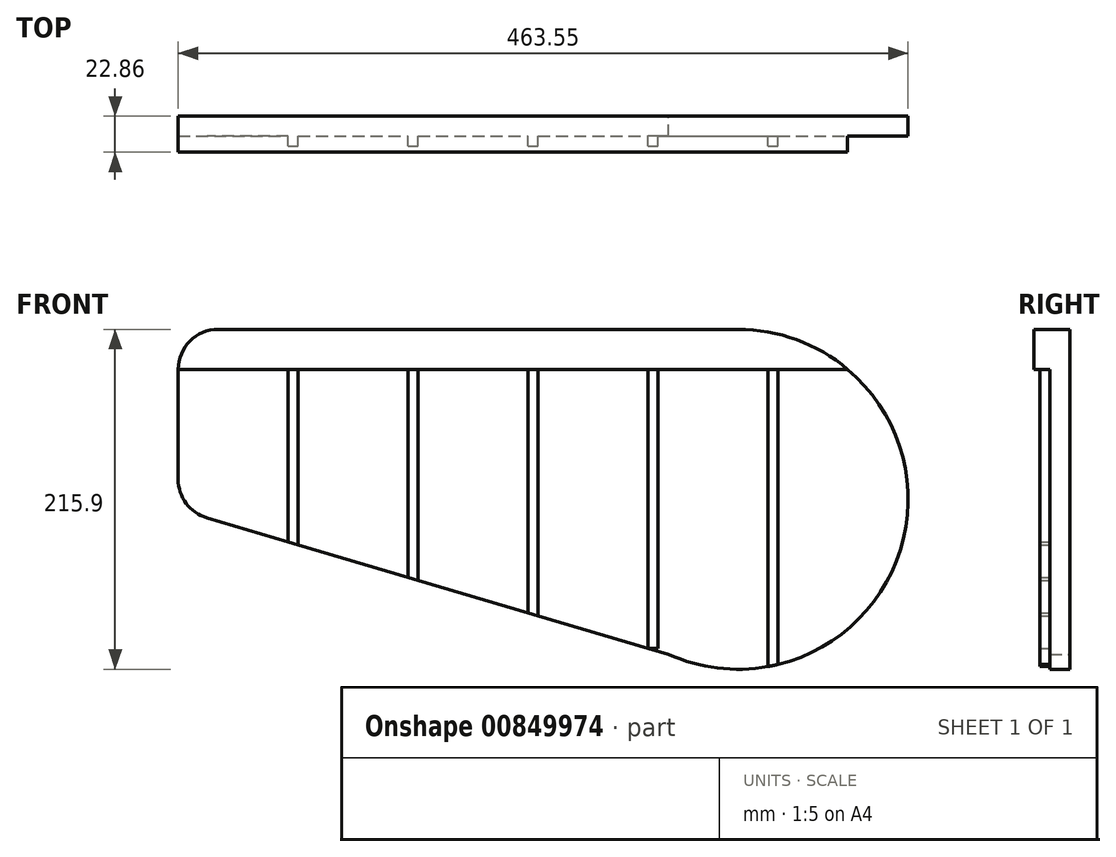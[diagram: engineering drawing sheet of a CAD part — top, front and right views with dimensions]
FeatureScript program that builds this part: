
annotation { "Feature Type Name" : "Feature", "Feature Type Description" : "" }
export const myFeature = defineFeature(function(context is Context, id is Id, definition is map)
    precondition{}
    {
        {
            var Q0;
            Q0=qCreatedBy(makeId("Front.planeOp"),FACE);
            var sketch = newSketch(context, id + "F0", { "sketchPlane" : qUnion([Q0])});
            skLineSegment(sketch, "E0", {"start": v(0, 18.97) * mm, "end": v(0, 88.9) * mm});
            skLineSegment(sketch, "E1", {"start": v(25.4, 114.3) * mm, "end": v(355.6, 114.3) * mm});
            skLineSegment(sketch, "E2", {"start": v(311.37, -92.12) * mm, "end": v(18.2, -5.38) * mm});
            skArc(sketch, "E3", {"start": v(311.37, -92.12) * mm, "mid": v(461.15, -16.27) * mm, "end": v(355.6, 114.3) * mm});
            skPoint(sketch, "E4.visualSharp", {"position": v(0, 114.3) * mm});
            skArc(sketch, "E4.filletArc", {"start": v(25.4, 114.3) * mm, "mid": v(7.44, 106.86) * mm, "end": v(0, 88.9) * mm});
            skPoint(sketch, "E5.visualSharp", {"position": v(0, 0) * mm});
            skArc(sketch, "E5.filletArc", {"start": v(0, 18.97) * mm, "mid": v(5.05, 3.77) * mm, "end": v(18.2, -5.38) * mm});
            skSolve(sketch);
        }
        {
            var Q0;
            Q0=makeQuery(id+"F0.imprint","IMPRINT",FACE,{"disambiguationData":[TD([[makeQuery(id+"F0.imprint","IMPRINT",EDGE,{"derivedFrom":sQuery(id+"F0.wireOp",EDGE,"E0")}),-1.0]])]});
            extrude(context, id + "F1", {"entities" : qUnion([Q0]), "depth" : 12.7 * mm, "offsetDistance" : 25.4 * mm});
        }
        {
            var Q0;
            Q0=makeQuery(id+"F1.opExtrude","CAP_FACE",FACE,{"disambiguationData":[OSD([sQuery(id+"F0.wireOp",EDGE,"E0"),sQuery(id+"F0.wireOp",EDGE,"E1"),sQuery(id+"F0.wireOp",EDGE,"E2"),sQuery(id+"F0.wireOp",EDGE,"E3"),sQuery(id+"F0.wireOp",EDGE,"E4.filletArc"),sQuery(id+"F0.wireOp",EDGE,"E5.filletArc")])],"isStart":false});
            var sketch = newSketch(context, id + "F2", { "sketchPlane" : qUnion([Q0])});
            skLineSegment(sketch, "E6", {"start": v(0, 88.9) * mm, "end": v(425.16, 88.9) * mm});
            skSolve(sketch);
        }
        {
            var Q0;
            {var subQ0=sQuery(id+"F2.wireOp",EDGE,"E6");Q0=makeQuery(id+"F2.imprint","IMPRINT",FACE,{"disambiguationData":[TD([[makeQuery(id+"F2.imprint","IMPRINT",EDGE,{"derivedFrom":subQ0}),1.0]])]});}
            extrude(context, id + "F3", {"entities" : qUnion([Q0]), "operationType" : NewBodyOperationType.ADD, "depth" : 10.16 * mm, "offsetDistance" : 25.4 * mm});
        }
        {
            var Q0;
            Q0=makeQuery(id+"F1.opExtrude","CAP_FACE",FACE,{"disambiguationData":[OSD([sQuery(id+"F0.wireOp",EDGE,"E0"),sQuery(id+"F0.wireOp",EDGE,"E1"),sQuery(id+"F0.wireOp",EDGE,"E2"),sQuery(id+"F0.wireOp",EDGE,"E3"),sQuery(id+"F0.wireOp",EDGE,"E4.filletArc"),sQuery(id+"F0.wireOp",EDGE,"E5.filletArc")])],"isStart":false});
            var sketch = newSketch(context, id + "F4", { "sketchPlane" : qUnion([Q0])});
            skPoint(sketch, "E7", {"position": v(0, 88.9) * mm});
            skPoint(sketch, "E8", {"position": v(69.85, 88.9) * mm});
            skPoint(sketch, "E9", {"position": v(76.2, 88.9) * mm});
            skPoint(sketch, "E10", {"position": v(146.05, 88.9) * mm});
            skPoint(sketch, "E11", {"position": v(152.4, 88.9) * mm});
            skPoint(sketch, "E12", {"position": v(222.25, 88.9) * mm});
            skPoint(sketch, "E13", {"position": v(228.6, 88.9) * mm});
            skPoint(sketch, "E14", {"position": v(298.45, 88.9) * mm});
            skPoint(sketch, "E15", {"position": v(304.8, 88.9) * mm});
            skPoint(sketch, "E16", {"position": v(374.65, 88.9) * mm});
            skPoint(sketch, "E17", {"position": v(381, 88.9) * mm});
            skLineSegment(sketch, "E18", {"start": v(69.85, 88.9) * mm, "end": v(76.2, 88.9) * mm});
            skLineSegment(sketch, "E19", {"start": v(69.85, 88.9) * mm, "end": v(69.85, -20.67) * mm});
            skLineSegment(sketch, "E20", {"start": v(76.2, 88.9) * mm, "end": v(76.2, -22.54) * mm});
            skLineSegment(sketch, "E21", {"start": v(69.85, -20.67) * mm, "end": v(76.2, -22.54) * mm});
            skLineSegment(sketch, "E22", {"start": v(146.05, 88.9) * mm, "end": v(146.05, -43.21) * mm});
            skLineSegment(sketch, "E23", {"start": v(152.4, 88.9) * mm, "end": v(152.4, -45.09) * mm});
            skLineSegment(sketch, "E24", {"start": v(152.4, -45.09) * mm, "end": v(146.05, -43.21) * mm});
            skLineSegment(sketch, "E25", {"start": v(222.25, 88.9) * mm, "end": v(222.25, -65.76) * mm});
            skLineSegment(sketch, "E26", {"start": v(228.6, 88.9) * mm, "end": v(228.6, -67.63) * mm});
            skLineSegment(sketch, "E27", {"start": v(228.6, -67.63) * mm, "end": v(222.25, -65.76) * mm});
            skLineSegment(sketch, "E28", {"start": v(298.45, 88.9) * mm, "end": v(298.45, -88.3) * mm});
            skLineSegment(sketch, "E29", {"start": v(304.8, 88.9) * mm, "end": v(304.8, -88.3) * mm});
            skLineSegment(sketch, "E30", {"start": v(304.8, -88.3) * mm, "end": v(298.45, -88.3) * mm});
            skLineSegment(sketch, "E31", {"start": v(374.65, 88.9) * mm, "end": v(374.65, -99.9) * mm});
            skLineSegment(sketch, "E32", {"start": v(381, 88.9) * mm, "end": v(381, -98.57) * mm});
            skLineSegment(sketch, "E33", {"start": v(374.65, -99.9) * mm, "end": v(381, -98.57) * mm});
            skSolve(sketch);
        }
        {
            var Q0;
            Q0=makeQuery(id+"F4.imprint","IMPRINT",FACE,{"disambiguationData":[TD([[makeQuery(id+"F4.imprint","IMPRINT",EDGE,{"derivedFrom":sQuery(id+"F4.wireOp",EDGE,"E18")}),-1.0]])]});
            var Q1;
            {var subQ0=sQuery(id+"F4.wireOp",EDGE,"E22");Q1=makeQuery(id+"F4.imprint","IMPRINT",FACE,{"disambiguationData":[TD([[makeQuery(id+"F4.imprint","IMPRINT",EDGE,{"derivedFrom":subQ0}),1.0]])]});}
            var Q2;
            {var subQ0=sQuery(id+"F4.wireOp",EDGE,"E25");Q2=makeQuery(id+"F4.imprint","IMPRINT",FACE,{"disambiguationData":[TD([[makeQuery(id+"F4.imprint","IMPRINT",EDGE,{"derivedFrom":subQ0}),1.0]])]});}
            var Q3;
            {var subQ0=sQuery(id+"F4.wireOp",EDGE,"E28");Q3=makeQuery(id+"F4.imprint","IMPRINT",FACE,{"disambiguationData":[TD([[makeQuery(id+"F4.imprint","IMPRINT",EDGE,{"derivedFrom":subQ0}),1.0]])]});}
            var Q4;
            {var subQ0=sQuery(id+"F4.wireOp",EDGE,"E31");Q4=makeQuery(id+"F4.imprint","IMPRINT",FACE,{"disambiguationData":[TD([[makeQuery(id+"F4.imprint","IMPRINT",EDGE,{"derivedFrom":subQ0}),1.0]])]});}
            extrude(context, id + "F5", {"entities" : qUnion([Q0, Q1, Q2, Q3, Q4]), "operationType" : NewBodyOperationType.ADD, "depth" : 6.35 * mm, "offsetDistance" : 25.4 * mm});
        }
    });
